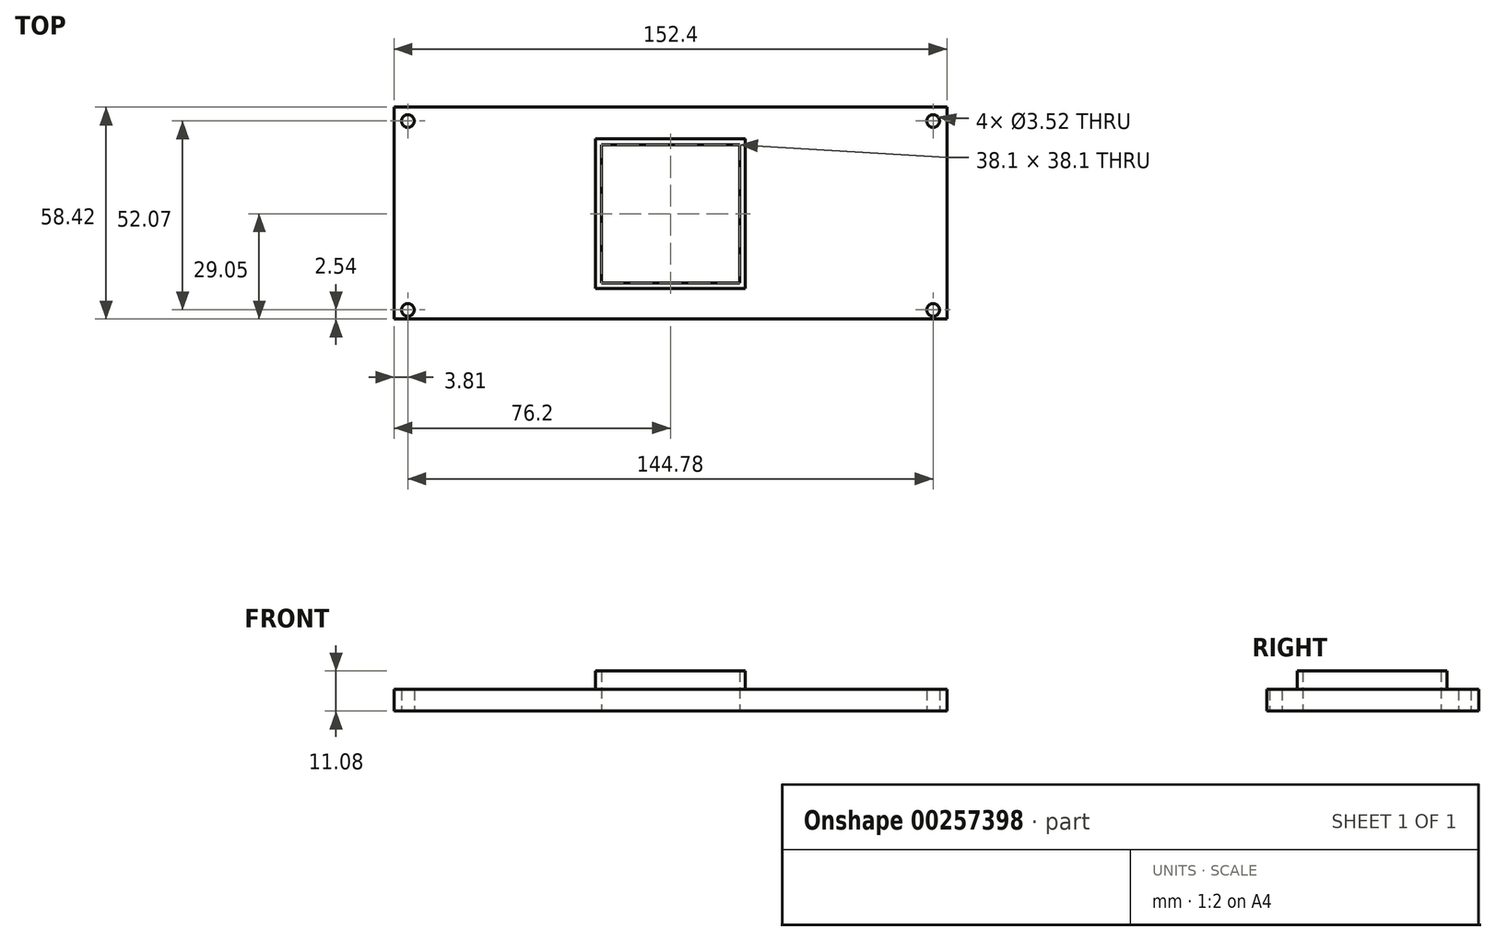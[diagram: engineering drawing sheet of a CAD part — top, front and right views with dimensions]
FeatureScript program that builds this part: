
annotation { "Feature Type Name" : "Feature", "Feature Type Description" : "" }
export const myFeature = defineFeature(function(context is Context, id is Id, definition is map)
    precondition{}
    {
        {
            var Q0;
            Q0=qCreatedBy(makeId("Top.planeOp"),FACE);
            var sketch = newSketch(context, id + "F0", { "sketchPlane" : qUnion([Q0])});
            skLineSegment(sketch, "E0.bottom", {"start": v(0, 58.42) * mm, "end": v(152.4, 58.42) * mm});
            skLineSegment(sketch, "E0.top", {"start": v(0, 0) * mm, "end": v(152.4, 0) * mm});
            skLineSegment(sketch, "E0.left", {"start": v(0, 58.42) * mm, "end": v(0, 0) * mm});
            skLineSegment(sketch, "E0.right", {"start": v(152.4, 58.42) * mm, "end": v(152.4, 0) * mm});
            skPoint(sketch, "E1", {"position": v(3.81, 54.61) * mm});
            skPoint(sketch, "E2", {"position": v(3.81, 2.54) * mm});
            skPoint(sketch, "E3", {"position": v(148.6, 2.54) * mm});
            skPoint(sketch, "E4", {"position": v(148.6, 54.61) * mm});
            skCircle(sketch, "E5", {"center": v(3.81, 2.54) * mm, "radius": 1.76 * mm});
            skCircle(sketch, "E6", {"center": v(3.81, 54.61) * mm, "radius": 1.76 * mm});
            skCircle(sketch, "E7", {"center": v(148.6, 54.61) * mm, "radius": 1.76 * mm});
            skCircle(sketch, "E8", {"center": v(148.6, 2.54) * mm, "radius": 1.76 * mm});
            skLineSegment(sketch, "E9.bottom", {"start": v(57.15, 48.1) * mm, "end": v(95.25, 48.1) * mm});
            skLineSegment(sketch, "E9.top", {"start": v(57.15, 10) * mm, "end": v(95.25, 10) * mm});
            skLineSegment(sketch, "E9.left", {"start": v(57.15, 48.1) * mm, "end": v(57.15, 10) * mm});
            skLineSegment(sketch, "E9.right", {"start": v(95.25, 48.1) * mm, "end": v(95.25, 10) * mm});
            skSolve(sketch);
        }
        {
            var Q0;
            Q0 = qSketchRegion(id + "F0", true);
            extrude(context, id + "F1", {"entities" : qUnion([Q0]), "depth" : 6 * mm});
        }
        {
            var Q0;
            Q0=makeQuery(id+"F1.opExtrude","CAP_FACE",FACE,{"disambiguationData":[OSD([sQuery(id+"F0.wireOp",EDGE,"E0.bottom"),sQuery(id+"F0.wireOp",EDGE,"E0.top"),sQuery(id+"F0.wireOp",EDGE,"E0.left"),sQuery(id+"F0.wireOp",EDGE,"E0.right"),sQuery(id+"F0.wireOp",EDGE,"E5"),sQuery(id+"F0.wireOp",EDGE,"E6"),sQuery(id+"F0.wireOp",EDGE,"E7"),sQuery(id+"F0.wireOp",EDGE,"E8"),sQuery(id+"F0.wireOp",EDGE,"E9.bottom"),sQuery(id+"F0.wireOp",EDGE,"E9.top"),sQuery(id+"F0.wireOp",EDGE,"E9.left"),sQuery(id+"F0.wireOp",EDGE,"E9.right")])],"isStart":false});
            var sketch = newSketch(context, id + "F2", { "sketchPlane" : qUnion([Q0])});
            skLineSegment(sketch, "E10", {"start": v(76.2, 48.1) * mm, "end": v(76.2, 10) * mm, "construction": true});
            skLineSegment(sketch, "E11.bottom", {"start": v(55.56, 49.69) * mm, "end": v(96.84, 49.69) * mm});
            skLineSegment(sketch, "E11.top", {"start": v(55.56, 8.41) * mm, "end": v(96.84, 8.41) * mm});
            skLineSegment(sketch, "E11.left", {"start": v(55.56, 49.69) * mm, "end": v(55.56, 8.41) * mm});
            skLineSegment(sketch, "E11.right", {"start": v(96.84, 49.69) * mm, "end": v(96.84, 8.41) * mm});
            skPoint(sketch, "E11.middle", {"position": v(76.2, 29.05) * mm});
            skLineSegment(sketch, "E12.bottom", {"start": v(57.15, 48.1) * mm, "end": v(95.25, 48.1) * mm});
            skLineSegment(sketch, "E12.top", {"start": v(57.15, 10) * mm, "end": v(95.25, 10) * mm});
            skLineSegment(sketch, "E12.left", {"start": v(57.15, 48.1) * mm, "end": v(57.15, 10) * mm});
            skLineSegment(sketch, "E12.right", {"start": v(95.25, 48.1) * mm, "end": v(95.25, 10) * mm});
            skSolve(sketch);
        }
        {
            var Q0;
            Q0 = qSketchRegion(id + "F2", true);
            extrude(context, id + "F3", {"entities" : qUnion([Q0]), "operationType" : NewBodyOperationType.ADD, "depth" : 5.08 * mm});
        }
    });
